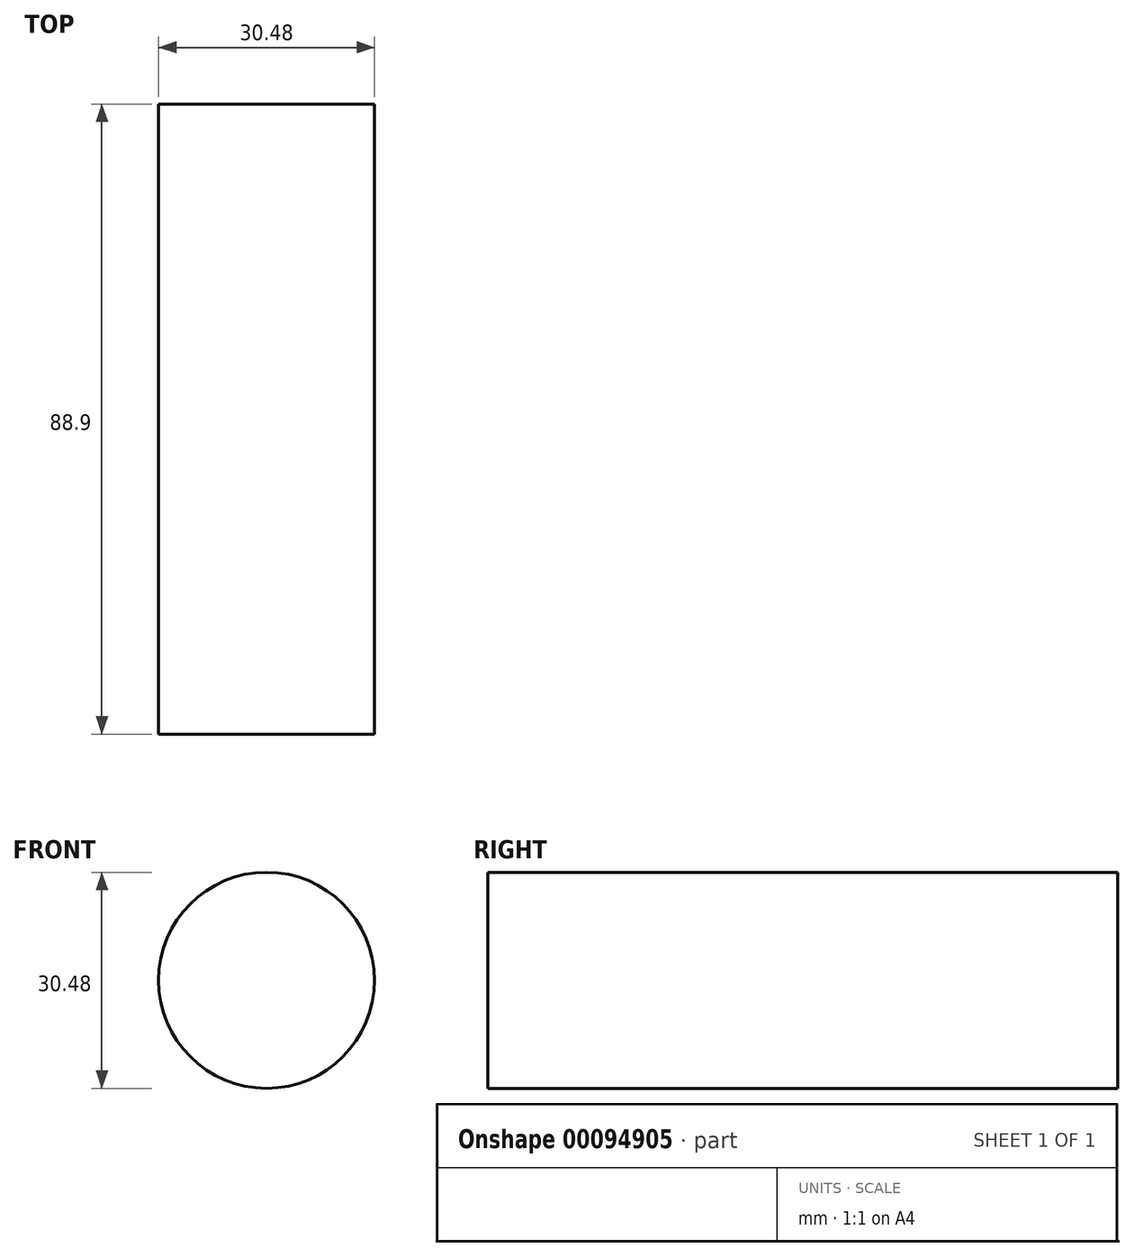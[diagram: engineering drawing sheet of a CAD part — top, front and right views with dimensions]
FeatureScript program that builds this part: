
annotation { "Feature Type Name" : "Feature", "Feature Type Description" : "" }
export const myFeature = defineFeature(function(context is Context, id is Id, definition is map)
    precondition{}
    {
        {
            var Q0;
            Q0=qCreatedBy(makeId("Front.planeOp"),FACE);
            var sketch = newSketch(context, id + "F0", { "sketchPlane" : qUnion([Q0])});
            skCircle(sketch, "E0", {"center": v(0, 0) * mm, "radius": 15.24 * mm});
            skSolve(sketch);
        }
        {
            var Q0;
            Q0=makeQuery(id+"F0.imprint","IMPRINT",FACE,{"disambiguationData":[TD([[makeQuery(id+"F0.imprint","IMPRINT",EDGE,{"derivedFrom":sQuery(id+"F0.wireOp",EDGE,"E0")}),1.0]])]});
            extrude(context, id + "F1", {"entities" : qUnion([Q0]), "depth" : 88.9 * mm});
        }
    });
